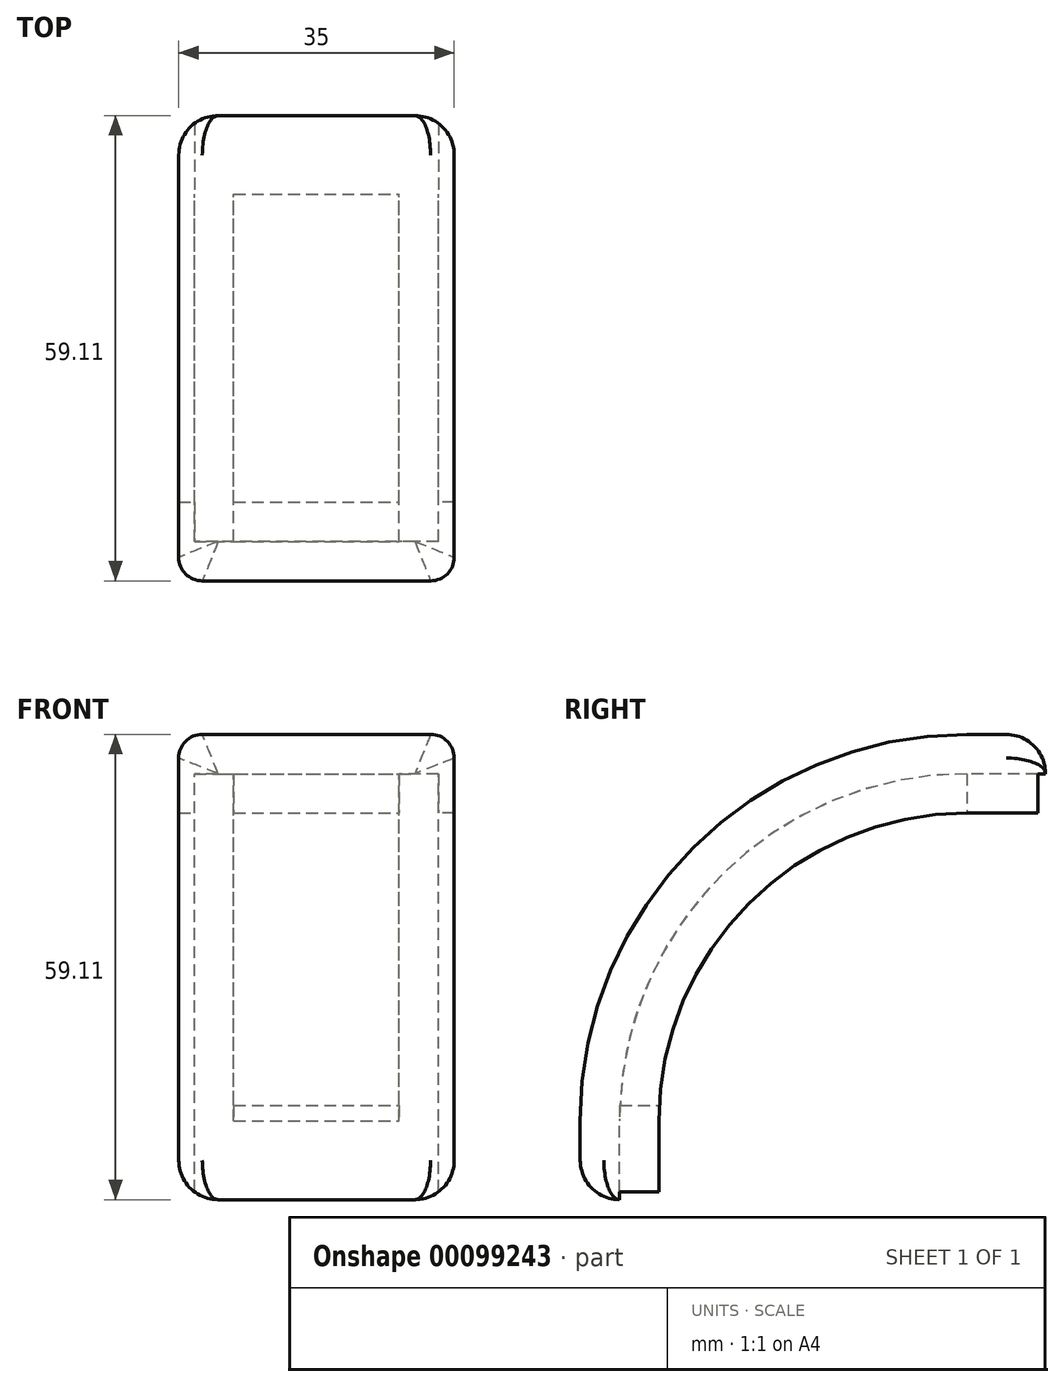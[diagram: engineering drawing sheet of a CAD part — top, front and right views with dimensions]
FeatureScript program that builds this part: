
annotation { "Feature Type Name" : "Feature", "Feature Type Description" : "" }
export const myFeature = defineFeature(function(context is Context, id is Id, definition is map)
    precondition{}
    {
        {
            var Q0;
            Q0=qCreatedBy(makeId("Front.planeOp"),FACE);
            var sketch = newSketch(context, id + "F0", { "sketchPlane" : qUnion([Q0])});
            skLineSegment(sketch, "E0.bottom", {"start": v(-17.5, 39.1) * mm, "end": v(-15.5, 39.1) * mm});
            skLineSegment(sketch, "E0.top", {"start": v(-14.5, 49.1) * mm, "end": v(14.5, 49.1) * mm});
            skLineSegment(sketch, "E0.left", {"start": v(-17.5, 39.1) * mm, "end": v(-17.5, 46.1) * mm});
            skLineSegment(sketch, "E0.right", {"start": v(17.5, 39.1) * mm, "end": v(17.5, 46.1) * mm});
            skPoint(sketch, "E0.middle", {"position": v(0, 44.1) * mm});
            skPoint(sketch, "E1.visualSharp", {"position": v(-17.5, 49.1) * mm});
            skArc(sketch, "E1.filletArc", {"start": v(-14.5, 49.1) * mm, "mid": v(-16.62, 48.23) * mm, "end": v(-17.5, 46.1) * mm});
            skPoint(sketch, "E2.visualSharp", {"position": v(17.5, 49.1) * mm});
            skArc(sketch, "E2.filletArc", {"start": v(17.5, 46.1) * mm, "mid": v(16.62, 48.23) * mm, "end": v(14.5, 49.1) * mm});
            skLineSegment(sketch, "E3", {"start": v(-15.5, 39.1) * mm, "end": v(-15.5, 44.1) * mm});
            skLineSegment(sketch, "E4", {"start": v(-15.5, 44.1) * mm, "end": v(-10.5, 44.1) * mm});
            skLineSegment(sketch, "E5", {"start": v(-10.5, 44.1) * mm, "end": v(-10.5, 39.1) * mm});
            skLineSegment(sketch, "E6", {"start": v(17.5, 39.1) * mm, "end": v(15.5, 39.1) * mm});
            skLineSegment(sketch, "E7", {"start": v(15.5, 39.1) * mm, "end": v(15.5, 44.1) * mm});
            skLineSegment(sketch, "E8", {"start": v(15.5, 44.1) * mm, "end": v(10.5, 44.1) * mm});
            skLineSegment(sketch, "E9", {"start": v(10.5, 44.1) * mm, "end": v(10.5, 39.1) * mm});
            skLineSegment(sketch, "E10.trimOffspring", {"start": v(-10.5, 39.1) * mm, "end": v(10.5, 39.1) * mm});
            skLineSegment(sketch, "E11.trimOffspring", {"start": v(15.5, 39.1) * mm, "end": v(17.5, 39.1) * mm});
            skLineSegment(sketch, "E12", {"start": v(-22.88, 0) * mm, "end": v(30.33, 0) * mm});
            skLineSegment(sketch, "E13", {"start": v(0, 39.1) * mm, "end": v(0, 0) * mm});
            skLineSegment(sketch, "E14", {"start": v(0, 49.1) * mm, "end": v(0, 0) * mm});
            skSolve(sketch);
        }
        {
            var Q0;
            Q0=makeQuery(id+"F0.imprint","IMPRINT",FACE,{"disambiguationData":[TD([[makeQuery(id+"F0.imprint","IMPRINT",EDGE,{"derivedFrom":sQuery(id+"F0.wireOp",EDGE,"E0.top")}),-1.0]])]});
            var Q1;
            Q1=sQuery(id+"F0.wireOp",EDGE,"E12");
            revolve(context, id + "F1", {"entities" : qUnion([Q0]), "axis" : qUnion([Q1]), "revolveType" : RevolveType.ONE_DIRECTION, "angle" : 90 * degree});
        }
        {
            var Q0;
            Q0=makeQuery(id+"F1.opRevolve","CAP_FACE",FACE,{"disambiguationData":[OSD([sQuery(id+"F0.wireOp",EDGE,"E0.top"),sQuery(id+"F0.wireOp",EDGE,"E0.left"),sQuery(id+"F0.wireOp",EDGE,"E0.right"),sQuery(id+"F0.wireOp",EDGE,"E1.filletArc"),sQuery(id+"F0.wireOp",EDGE,"E2.filletArc"),sQuery(id+"F0.wireOp",EDGE,"E0.bottom"),sQuery(id+"F0.wireOp",EDGE,"E3"),sQuery(id+"F0.wireOp",EDGE,"E4"),sQuery(id+"F0.wireOp",EDGE,"E5"),sQuery(id+"F0.wireOp",EDGE,"E7"),sQuery(id+"F0.wireOp",EDGE,"E8"),sQuery(id+"F0.wireOp",EDGE,"E9"),sQuery(id+"F0.wireOp",EDGE,"E10.trimOffspring"),sQuery(id+"F0.wireOp",EDGE,"E11.trimOffspring")])],"isStart":true});
            var sketch = newSketch(context, id + "F2", { "sketchPlane" : qUnion([Q0])});
            skLineSegment(sketch, "E15", {"start": v(-10.5, 39.1) * mm, "end": v(-10.5, 44.1) * mm});
            skLineSegment(sketch, "E16", {"start": v(-10.5, 44.1) * mm, "end": v(10.5, 44.1) * mm});
            skLineSegment(sketch, "E17", {"start": v(10.5, 44.1) * mm, "end": v(10.5, 39.1) * mm});
            skLineSegment(sketch, "E18", {"start": v(10.5, 39.1) * mm, "end": v(-10.5, 39.1) * mm});
            skSolve(sketch);
        }
        {
            var Q0;
            Q0=makeQuery(id+"F1.opRevolve","CAP_FACE",FACE,{"disambiguationData":[OSD([sQuery(id+"F0.wireOp",EDGE,"E0.top"),sQuery(id+"F0.wireOp",EDGE,"E0.left"),sQuery(id+"F0.wireOp",EDGE,"E0.right"),sQuery(id+"F0.wireOp",EDGE,"E1.filletArc"),sQuery(id+"F0.wireOp",EDGE,"E2.filletArc"),sQuery(id+"F0.wireOp",EDGE,"E0.bottom"),sQuery(id+"F0.wireOp",EDGE,"E3"),sQuery(id+"F0.wireOp",EDGE,"E4"),sQuery(id+"F0.wireOp",EDGE,"E5"),sQuery(id+"F0.wireOp",EDGE,"E7"),sQuery(id+"F0.wireOp",EDGE,"E8"),sQuery(id+"F0.wireOp",EDGE,"E9"),sQuery(id+"F0.wireOp",EDGE,"E10.trimOffspring"),sQuery(id+"F0.wireOp",EDGE,"E11.trimOffspring")])],"isStart":false});
            extrude(context, id + "F3", {"entities" : qUnion([Q0]), "operationType" : NewBodyOperationType.ADD, "depth" : 10 * mm});
        }
        {
            var Q0;
            Q0=makeQuery(id+"F2.imprint","IMPRINT",FACE,{"disambiguationData":[TD([[makeQuery(id+"F2.imprint","IMPRINT",EDGE,{"derivedFrom":sQuery(id+"F2.wireOp",EDGE,"E16")}),1.0]])]});
            var Q1;
            Q1=makeQuery(id+"F2.imprint","IMPRINT",FACE,{"disambiguationData":[TD([[makeQuery(id+"F2.imprint","IMPRINT",EDGE,{"derivedFrom":sQuery(id+"F2.wireOp",EDGE,"E15")}),1.0]])]});
            extrude(context, id + "F4", {"entities" : qUnion([Q0, Q1]), "operationType" : NewBodyOperationType.ADD, "depth" : 10 * mm});
        }
        {
            var Q0;
            Q0=makeQuery(id+"F3.opExtrude","CAP_FACE",FACE,{"disambiguationData":[OSD([sQuery(id+"F0.wireOp",EDGE,"E0.top"),sQuery(id+"F0.wireOp",EDGE,"E0.left"),sQuery(id+"F0.wireOp",EDGE,"E0.right"),sQuery(id+"F0.wireOp",EDGE,"E1.filletArc"),sQuery(id+"F0.wireOp",EDGE,"E2.filletArc"),sQuery(id+"F0.wireOp",EDGE,"E0.bottom"),sQuery(id+"F0.wireOp",EDGE,"E3"),sQuery(id+"F0.wireOp",EDGE,"E4"),sQuery(id+"F0.wireOp",EDGE,"E5"),sQuery(id+"F0.wireOp",EDGE,"E7"),sQuery(id+"F0.wireOp",EDGE,"E8"),sQuery(id+"F0.wireOp",EDGE,"E9"),sQuery(id+"F0.wireOp",EDGE,"E10.trimOffspring"),sQuery(id+"F0.wireOp",EDGE,"E11.trimOffspring")])],"isStart":false});
            var sketch = newSketch(context, id + "F5", { "sketchPlane" : qUnion([Q0])});
            skLineSegment(sketch, "E19", {"start": v(-10.5, 44.1) * mm, "end": v(-10.5, 39.1) * mm});
            skLineSegment(sketch, "E20", {"start": v(10.5, 39.1) * mm, "end": v(-10.5, 39.1) * mm});
            skLineSegment(sketch, "E21", {"start": v(-10.5, 44.1) * mm, "end": v(10.5, 44.1) * mm});
            skLineSegment(sketch, "E22", {"start": v(10.42, 43.98) * mm, "end": v(10.5, 41.6) * mm});
            skLineSegment(sketch, "E23", {"start": v(10.5, 44.1) * mm, "end": v(10.5, 39.1) * mm});
            skSolve(sketch);
        }
        {
            var Q0;
            Q0=makeQuery(id+"F5.imprint","IMPRINT",FACE,{"disambiguationData":[TD([[makeQuery(id+"F5.imprint","IMPRINT",EDGE,{"derivedFrom":sQuery(id+"F5.wireOp",EDGE,"E19")}),1.0]])]});
            extrude(context, id + "F6", {"entities" : qUnion([Q0]), "operationType" : NewBodyOperationType.REMOVE, "oppositeDirection" : true, "depth" : 12 * mm});
        }
        {
            var Q0;
            Q0=makeQuery(id+"F4.opExtrude","CAP_FACE",FACE,{"disambiguationData":[OSD([sQuery(id+"F0.wireOp",EDGE,"E0.top"),sQuery(id+"F0.wireOp",EDGE,"E0.left"),sQuery(id+"F0.wireOp",EDGE,"E0.right"),sQuery(id+"F0.wireOp",EDGE,"E1.filletArc"),sQuery(id+"F0.wireOp",EDGE,"E2.filletArc"),sQuery(id+"F0.wireOp",EDGE,"E0.bottom"),sQuery(id+"F0.wireOp",EDGE,"E3"),sQuery(id+"F0.wireOp",EDGE,"E4"),sQuery(id+"F0.wireOp",EDGE,"E7"),sQuery(id+"F0.wireOp",EDGE,"E8"),sQuery(id+"F0.wireOp",EDGE,"E11.trimOffspring"),sQuery(id+"F2.wireOp",EDGE,"E15"),sQuery(id+"F2.wireOp",EDGE,"E17"),sQuery(id+"F2.wireOp",EDGE,"E18")])],"isStart":false});
            var sketch = newSketch(context, id + "F7", { "sketchPlane" : qUnion([Q0])});
            skLineSegment(sketch, "E24", {"start": v(-10.5, 44.1) * mm, "end": v(-10.5, 39.1) * mm});
            skLineSegment(sketch, "E25", {"start": v(10.5, 39.1) * mm, "end": v(10.5, 44.1) * mm});
            skLineSegment(sketch, "E26", {"start": v(10.5, 44.1) * mm, "end": v(-10.5, 44.1) * mm});
            skLineSegment(sketch, "E27", {"start": v(10.5, 39.1) * mm, "end": v(-10.5, 39.1) * mm});
            skSolve(sketch);
        }
        {
            var Q0;
            Q0=makeQuery(id+"F7.imprint","IMPRINT",FACE,{"disambiguationData":[TD([[makeQuery(id+"F7.imprint","IMPRINT",EDGE,{"derivedFrom":sQuery(id+"F7.wireOp",EDGE,"E24")}),1.0]])]});
            extrude(context, id + "F8", {"entities" : qUnion([Q0]), "operationType" : NewBodyOperationType.REMOVE, "oppositeDirection" : true, "depth" : 10 * mm});
        }
        {
            var Q0;
            Q0=makeQuery(id+"F4.opExtrude","CAP_EDGE",EDGE,{"disambiguationData":[OSD([sQuery(id+"F0.wireOp",EDGE,"E0.top")])],"isStart":false});
            var Q1;
            Q1=makeQuery(id+"F4.opExtrude","CAP_EDGE",EDGE,{"disambiguationData":[OSD([sQuery(id+"F0.wireOp",EDGE,"E2.filletArc")])],"isStart":false});
            var Q2;
            Q2=makeQuery(id+"F4.opExtrude","CAP_EDGE",EDGE,{"disambiguationData":[OSD([sQuery(id+"F0.wireOp",EDGE,"E0.right")])],"isStart":false});
            var Q3;
            Q3=makeQuery(id+"F4.opExtrude","CAP_EDGE",EDGE,{"disambiguationData":[OSD([sQuery(id+"F0.wireOp",EDGE,"E1.filletArc")])],"isStart":false});
            var Q4;
            Q4=makeQuery(id+"F4.opExtrude","CAP_EDGE",EDGE,{"disambiguationData":[OSD([sQuery(id+"F0.wireOp",EDGE,"E0.left")])],"isStart":false});
            fillet(context, id + "F9", {"entities" : qUnion([Q0, Q1, Q2, Q3, Q4]), "radius" : 5 * mm, "tangentPropagation" : true, "allowEdgeOverflow" : false});
        }
        {
            var Q0;
            Q0=makeQuery(id+"F3.opExtrude","CAP_EDGE",EDGE,{"disambiguationData":[OSD([sQuery(id+"F0.wireOp",EDGE,"E0.top")])],"isStart":false});
            var Q1;
            Q1=makeQuery(id+"F3.opExtrude","CAP_EDGE",EDGE,{"disambiguationData":[OSD([sQuery(id+"F0.wireOp",EDGE,"E2.filletArc")])],"isStart":false});
            var Q2;
            Q2=makeQuery(id+"F3.opExtrude","CAP_EDGE",EDGE,{"disambiguationData":[OSD([sQuery(id+"F0.wireOp",EDGE,"E0.left")])],"isStart":false});
            var Q3;
            Q3=makeQuery(id+"F3.opExtrude","CAP_EDGE",EDGE,{"disambiguationData":[OSD([sQuery(id+"F0.wireOp",EDGE,"E1.filletArc")])],"isStart":false});
            var Q4;
            Q4=makeQuery(id+"F3.opExtrude","CAP_EDGE",EDGE,{"disambiguationData":[OSD([sQuery(id+"F0.wireOp",EDGE,"E0.right")])],"isStart":false});
            fillet(context, id + "F10", {"entities" : qUnion([Q0, Q1, Q2, Q3, Q4]), "radius" : 5 * mm, "tangentPropagation" : true, "allowEdgeOverflow" : false});
        }
    });
